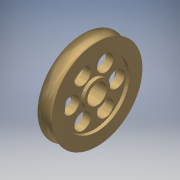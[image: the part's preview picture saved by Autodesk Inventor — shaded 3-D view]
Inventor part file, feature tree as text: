
AUTODESK INVENTOR PART (.ipt)
format: ipt  version: 2019 (Build 230136000, 136)  size: 164,352 bytes
history: imported  units: in
note: dims shown in document units (in); Inventor stores cm internally (conversion verified against a paired STEP export)
features: imported_body x1
ambient origin geometry x8: Origin, YZ Plane, XZ Plane, XY Plane, X Axis, Y Axis, Z Axis, Center Point
bodies: Solid1 (imported_parasolid), Body1 (imported_parasolid)
feature tree (1):
  imported_body  NMx_Import_Brep_tag  [imported B-rep: ~18 faces, bbox_mm=[2.2, 6.062178, 10.5]]
